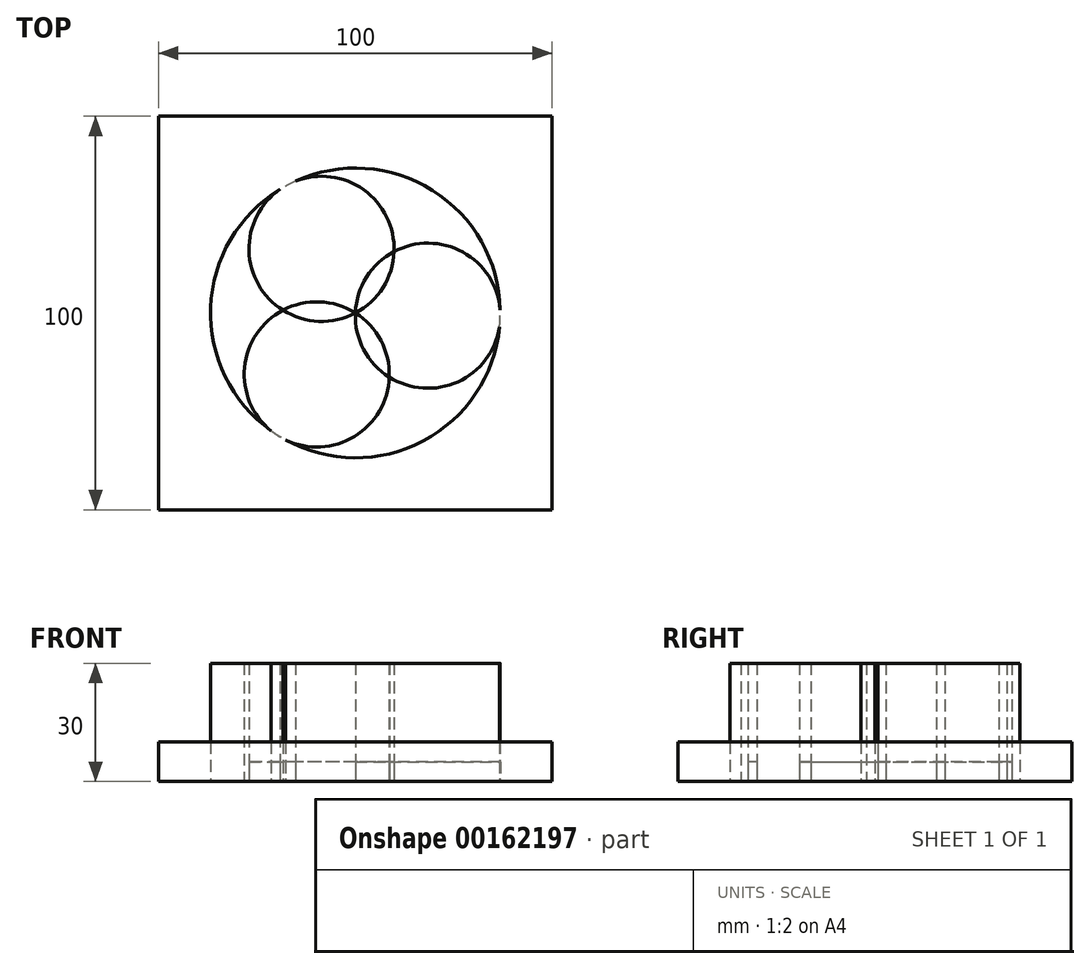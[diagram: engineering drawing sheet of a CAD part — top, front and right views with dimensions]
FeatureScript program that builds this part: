
annotation { "Feature Type Name" : "Feature", "Feature Type Description" : "" }
export const myFeature = defineFeature(function(context is Context, id is Id, definition is map)
    precondition{}
    {
        {
            var Q0;
            Q0=qCreatedBy(makeId("Top.planeOp"),FACE);
            var sketch = newSketch(context, id + "F0", { "sketchPlane" : qUnion([Q0])});
            skCircle(sketch, "E0", {"center": v(18.42, -0.7) * mm, "radius": 18.43 * mm});
            skPoint(sketch, "E0.first.point", {"position": v(0, -1.4) * mm});
            skPoint(sketch, "E0.second.point", {"position": v(36.84, 0) * mm});
            skPoint(sketch, "E0.third.point", {"position": v(0, 0) * mm});
            skCircle(sketch, "E1.1.0", {"center": v(-8.6, 16.3) * mm, "radius": 18.43 * mm});
            skCircle(sketch, "E1.2.0", {"center": v(-9.82, -15.6) * mm, "radius": 18.43 * mm});
            skCircle(sketch, "E2", {"center": v(0, 0) * mm, "radius": 36.8 * mm});
            skSolve(sketch);
        }
        {
            var Q0;
            {var subQ0=sQuery(id+"F0.wireOp",EDGE,"E1.2.0");var subQ1=sQuery(id+"F0.wireOp",EDGE,"E1.1.0");var subQ2=makeQuery(id+"F0.imprint","INTERSECT",VERTEX,{"derivedFrom":[subQ1,subQ0]});Q0=makeQuery(id+"F0.imprint","IMPRINT",FACE,{"disambiguationData":[TD([[makeQuery(id+"F0.imprint","IMPRINT",EDGE,{"disambiguationData":[TD([[subQ2,-1.0]])],"derivedFrom":subQ1}),1.0]])]});}
            var Q1;
            {var subQ0=sQuery(id+"F0.wireOp",EDGE,"E1.1.0");var subQ1=sQuery(id+"F0.wireOp",EDGE,"E0");var subQ2=makeQuery(id+"F0.imprint","INTERSECT",VERTEX,{"derivedFrom":[subQ1,subQ0]});Q1=makeQuery(id+"F0.imprint","IMPRINT",FACE,{"disambiguationData":[TD([[makeQuery(id+"F0.imprint","IMPRINT",EDGE,{"disambiguationData":[TD([[subQ2,-1.0]])],"derivedFrom":subQ1}),1.0]])]});}
            var Q2;
            {var subQ0=sQuery(id+"F0.wireOp",EDGE,"E1.2.0");var subQ1=sQuery(id+"F0.wireOp",EDGE,"E0");var subQ2=makeQuery(id+"F0.imprint","INTERSECT",VERTEX,{"derivedFrom":[subQ1,subQ0]});Q2=makeQuery(id+"F0.imprint","IMPRINT",FACE,{"disambiguationData":[TD([[makeQuery(id+"F0.imprint","IMPRINT",EDGE,{"disambiguationData":[TD([[subQ2,1.0]])],"derivedFrom":subQ1}),1.0]])]});}
            var Q3;
            {var subQ0=sQuery(id+"F0.wireOp",EDGE,"E2");var subQ1=sQuery(id+"F0.wireOp",EDGE,"E1.1.0");var subQ2=makeQuery(id+"F0.imprint","INTERSECT",VERTEX,{"disambiguationData":[OD(0.0)],"derivedFrom":[subQ1,subQ0]});Q3=makeQuery(id+"F0.imprint","IMPRINT",FACE,{"disambiguationData":[TD([[makeQuery(id+"F0.imprint","IMPRINT",EDGE,{"disambiguationData":[TD([[subQ2,-1.0]])],"derivedFrom":subQ1}),-1.0]])]});}
            var Q4;
            {var subQ0=sQuery(id+"F0.wireOp",EDGE,"E2");var subQ1=sQuery(id+"F0.wireOp",EDGE,"E0");var subQ2=makeQuery(id+"F0.imprint","INTERSECT",VERTEX,{"disambiguationData":[OD(0.0)],"derivedFrom":[subQ1,subQ0]});Q4=makeQuery(id+"F0.imprint","IMPRINT",FACE,{"disambiguationData":[TD([[makeQuery(id+"F0.imprint","IMPRINT",EDGE,{"disambiguationData":[TD([[subQ2,-1.0]])],"derivedFrom":subQ1}),-1.0]])]});}
            var Q5;
            {var subQ0=sQuery(id+"F0.wireOp",EDGE,"E2");var subQ1=sQuery(id+"F0.wireOp",EDGE,"E0");var subQ2=makeQuery(id+"F0.imprint","INTERSECT",VERTEX,{"disambiguationData":[OD(1.0)],"derivedFrom":[subQ1,subQ0]});Q5=makeQuery(id+"F0.imprint","IMPRINT",FACE,{"disambiguationData":[TD([[makeQuery(id+"F0.imprint","IMPRINT",EDGE,{"disambiguationData":[TD([[subQ2,1.0]])],"derivedFrom":subQ1}),-1.0]])]});}
            extrude(context, id + "F1", {"entities" : qUnion([Q0, Q1, Q2, Q3, Q4, Q5]), "depth" : 30 * mm});
        }
        {
            var Q0;
            {var subQ1=sQuery(id+"F0.wireOp",EDGE,"E1.1.0");var subQ5=sQuery(id+"F0.wireOp",EDGE,"E2");var subQ6=makeQuery(id+"F0.imprint","INTERSECT",VERTEX,{"disambiguationData":[OD(0.0)],"derivedFrom":[subQ1,subQ5]});Q0=makeQuery(id+"F0.imprint","IMPRINT",FACE,{"disambiguationData":[TD([[makeQuery(id+"F0.imprint","IMPRINT",EDGE,{"disambiguationData":[TD([[subQ6,-1.0]])],"derivedFrom":subQ1}),1.0]])]});}
            var Q1;
            {var subQ0=sQuery(id+"F0.wireOp",EDGE,"E2");var subQ1=sQuery(id+"F0.wireOp",EDGE,"E1.2.0");var subQ7=makeQuery(id+"F0.imprint","INTERSECT",VERTEX,{"disambiguationData":[OD(0.0)],"derivedFrom":[subQ1,subQ0]});Q1=makeQuery(id+"F0.imprint","IMPRINT",FACE,{"disambiguationData":[TD([[makeQuery(id+"F0.imprint","IMPRINT",EDGE,{"disambiguationData":[TD([[subQ7,-1.0]])],"derivedFrom":subQ1}),1.0]])]});}
            var Q2;
            {var subQ1=sQuery(id+"F0.wireOp",EDGE,"E0");var subQ6=sQuery(id+"F0.wireOp",EDGE,"E2");var subQ8=makeQuery(id+"F0.imprint","INTERSECT",VERTEX,{"disambiguationData":[OD(0.0)],"derivedFrom":[subQ1,subQ6]});Q2=makeQuery(id+"F0.imprint","IMPRINT",FACE,{"disambiguationData":[TD([[makeQuery(id+"F0.imprint","IMPRINT",EDGE,{"disambiguationData":[TD([[subQ8,-1.0]])],"derivedFrom":subQ1}),1.0]])]});}
            extrude(context, id + "F2", {"entities" : qUnion([Q0, Q1, Q2]), "depth" : 5 * mm});
        }
        {
            var Q0;
            Q0=qCreatedBy(makeId("Top.planeOp"),FACE);
            var sketch = newSketch(context, id + "F3", { "sketchPlane" : qUnion([Q0])});
            skLineSegment(sketch, "E3.bottom", {"start": v(50, 50) * mm, "end": v(-50, 50) * mm});
            skLineSegment(sketch, "E3.top", {"start": v(50, -50) * mm, "end": v(-50, -50) * mm});
            skLineSegment(sketch, "E3.left", {"start": v(50, 50) * mm, "end": v(50, -50) * mm});
            skLineSegment(sketch, "E3.right", {"start": v(-50, 50) * mm, "end": v(-50, -50) * mm});
            skPoint(sketch, "E3.middle", {"position": v(0, 0) * mm});
            skSolve(sketch);
        }
        {
            var Q0;
            Q0=makeQuery(id+"F3.imprint","IMPRINT",FACE,{"disambiguationData":[TD([[makeQuery(id+"F3.imprint","IMPRINT",EDGE,{"derivedFrom":sQuery(id+"F3.wireOp",EDGE,"E3.bottom")}),1.0]])]});
            extrude(context, id + "F4", {"entities" : qUnion([Q0]), "depth" : 10 * mm});
        }
    });
